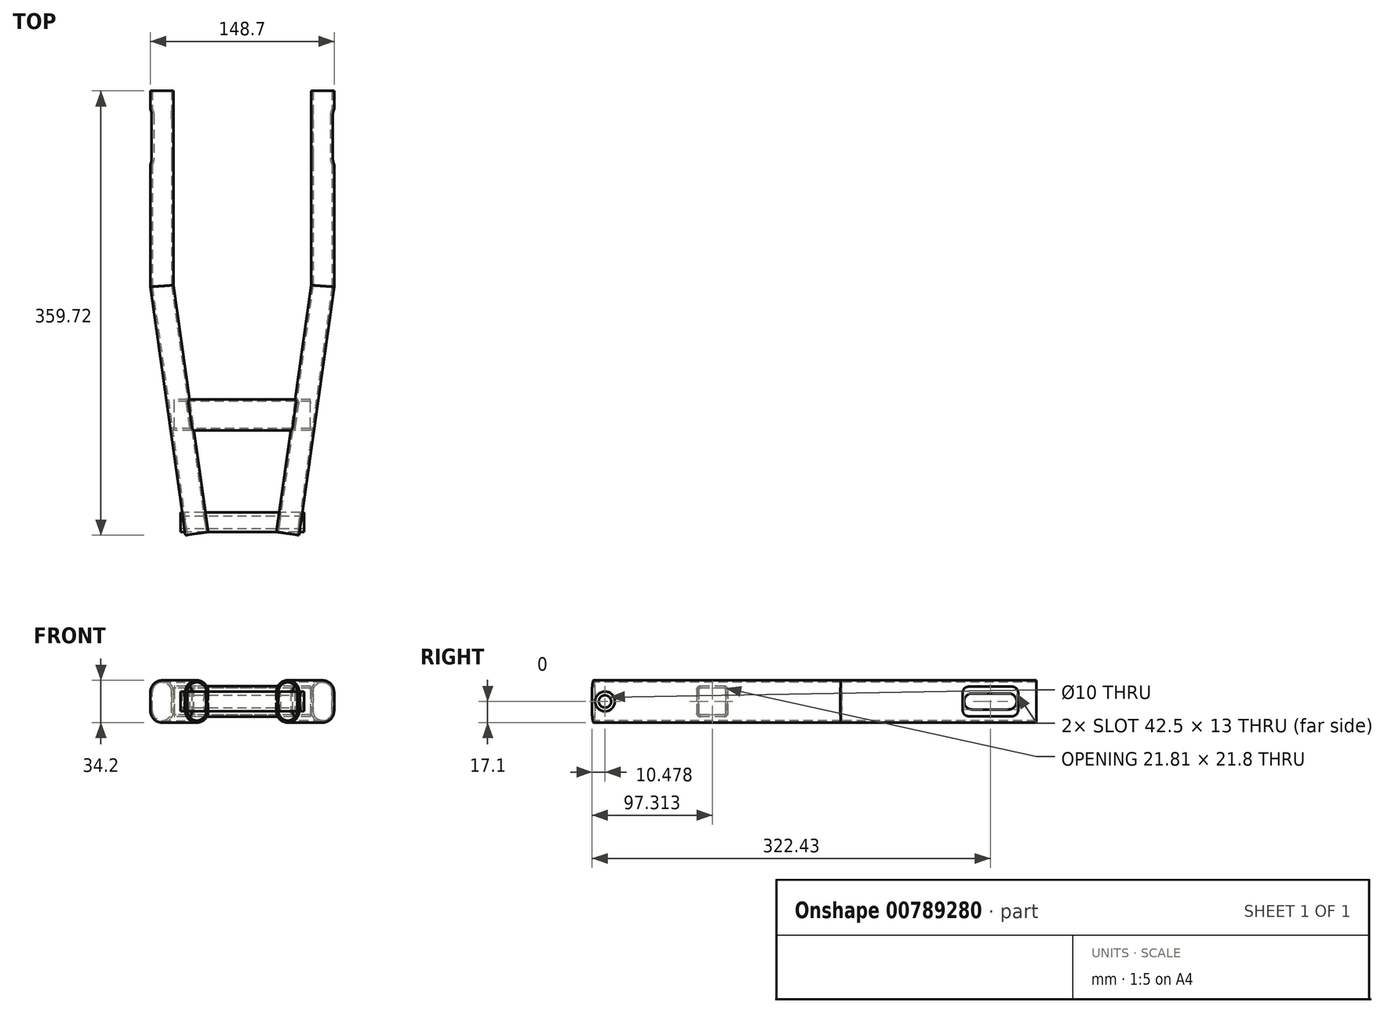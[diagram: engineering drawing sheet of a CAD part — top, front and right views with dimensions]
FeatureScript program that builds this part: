
annotation { "Feature Type Name" : "Feature", "Feature Type Description" : "" }
export const myFeature = defineFeature(function(context is Context, id is Id, definition is map)
    precondition{}
    {
        {
            var Q0;
            Q0=qCreatedBy(makeId("Front.planeOp"),FACE);
            var sketch = newSketch(context, id + "F0", { "sketchPlane" : qUnion([Q0])});
            skLineSegment(sketch, "E0.left", {"start": v(-57.25, -7.75) * mm, "end": v(-57.25, 7.75) * mm});
            skLineSegment(sketch, "E0.right", {"start": v(-72.75, -7.75) * mm, "end": v(-72.75, 7.75) * mm});
            skPoint(sketch, "E0.middle", {"position": v(-65, 0) * mm});
            skArc(sketch, "E1", {"start": v(-57.25, 7.75) * mm, "mid": v(-65, 15.5) * mm, "end": v(-72.75, 7.75) * mm});
            skArc(sketch, "E2", {"start": v(-72.75, -7.75) * mm, "mid": v(-65, -15.5) * mm, "end": v(-57.25, -7.75) * mm});
            skLineSegment(sketch, "E3", {"start": v(-55.65, 7.75) * mm, "end": v(-55.65, -7.75) * mm});
            skLineSegment(sketch, "E4", {"start": v(-74.35, 7.75) * mm, "end": v(-74.35, -7.75) * mm});
            skArc(sketch, "E5", {"start": v(-55.65, 7.75) * mm, "mid": v(-65, 17.1) * mm, "end": v(-74.35, 7.75) * mm});
            skArc(sketch, "E6", {"start": v(-74.35, -7.75) * mm, "mid": v(-65, -17.1) * mm, "end": v(-55.65, -7.75) * mm});
            skSolve(sketch);
        }
        {
            var Q0;
            Q0=qCreatedBy(makeId("Top.planeOp"),FACE);
            var sketch = newSketch(context, id + "F1", { "sketchPlane" : qUnion([Q0])});
            skLineSegment(sketch, "E7", {"start": v(-65, 0) * mm, "end": v(-65, -158.03) * mm});
            skLineSegment(sketch, "E8", {"start": v(-65, -158.03) * mm, "end": v(-36.84, -358.42) * mm});
            skSolve(sketch);
        }
        {
            var Q0;
            Q0 = qSketchRegion(id + "F0", true);
            var Q1;
            Q1=sQuery(id+"F1.wireOp",EDGE,"E7");
            var Q2;
            Q2=sQuery(id+"F1.wireOp",EDGE,"E8");
            sweep(context, id + "F2", {"profiles" : qUnion([Q0]), "path" : qUnion([Q1, Q2])});
        }
        {
            var Q0;
            Q0=makeQuery(id+"F2.opSweep","SWEPT_BODY",BODY,{"disambiguationData":[OSD([sQuery(id+"F0.wireOp",EDGE,"E0.left"),sQuery(id+"F0.wireOp",EDGE,"E0.right"),sQuery(id+"F0.wireOp",EDGE,"E1"),sQuery(id+"F0.wireOp",EDGE,"E2"),sQuery(id+"F0.wireOp",EDGE,"E3"),sQuery(id+"F0.wireOp",EDGE,"E4"),sQuery(id+"F0.wireOp",EDGE,"E5"),sQuery(id+"F0.wireOp",EDGE,"E6"),sQuery(id+"F1.wireOp",EDGE,"E8")])]});
            var Q1;
            Q1=qCreatedBy(makeId("Right.planeOp"),FACE);
            mirror(context, id + "F3", {"operationType" : NewBodyOperationType.ADD, "entities" : qUnion([Q0]), "mirrorPlane" : qUnion([Q1])});
        }
        {
            var Q0;
            Q0=qCreatedBy(makeId("Right.planeOp"),FACE);
            var sketch = newSketch(context, id + "F4", { "sketchPlane" : qUnion([Q0])});
            skCircle(sketch, "E9", {"center": v(-349.24, 0) * mm, "radius": 8 * mm});
            skSolve(sketch);
        }
        {
            var Q0;
            Q0 = qSketchRegion(id + "F4", true);
            extrude(context, id + "F5", {"entities" : qUnion([Q0]), "operationType" : NewBodyOperationType.ADD, "endBound" : BoundingType.SYMMETRIC, "depth" : 100 * mm, "offsetDistance" : 25 * mm});
        }
        {
            var Q0;
            Q0=makeQuery(id+"F5.opExtrude","CAP_FACE",FACE,{"disambiguationData":[OSD([sQuery(id+"F4.wireOp",EDGE,"E9")])],"isStart":false});
            var sketch = newSketch(context, id + "F6", { "sketchPlane" : qUnion([Q0])});
            skCircle(sketch, "E10", {"center": v(-349.24, 0) * mm, "radius": 5 * mm});
            skSolve(sketch);
        }
        {
            var Q0;
            Q0=makeQuery(id+"F6.imprint","IMPRINT",FACE,{"disambiguationData":[TD([[makeQuery(id+"F6.imprint","IMPRINT",EDGE,{"derivedFrom":sQuery(id+"F6.wireOp",EDGE,"E10")}),1.0]])]});
            extrude(context, id + "F7", {"entities" : qUnion([Q0]), "operationType" : NewBodyOperationType.REMOVE, "oppositeDirection" : true, "depth" : 100 * mm, "offsetDistance" : 25 * mm});
        }
        {
            var Q0;
            Q0=qCreatedBy(makeId("Right.planeOp"),FACE);
            var sketch = newSketch(context, id + "F8", { "sketchPlane" : qUnion([Q0])});
            skLineSegment(sketch, "E11.bottom", {"start": v(-271.91, 12.5) * mm, "end": v(-252.9, 12.5) * mm});
            skLineSegment(sketch, "E11.top", {"start": v(-271.91, -12.5) * mm, "end": v(-252.9, -12.5) * mm});
            skLineSegment(sketch, "E11.left", {"start": v(-274.91, 9.5) * mm, "end": v(-274.91, -9.5) * mm});
            skLineSegment(sketch, "E11.right", {"start": v(-249.9, 9.5) * mm, "end": v(-249.9, -9.5) * mm});
            skPoint(sketch, "E11.middle", {"position": v(-262.4, 0) * mm});
            skPoint(sketch, "E12.visualSharp", {"position": v(-249.9, 12.5) * mm});
            skArc(sketch, "E12.filletArc", {"start": v(-249.9, 9.5) * mm, "mid": v(-250.78, 11.62) * mm, "end": v(-252.9, 12.5) * mm});
            skPoint(sketch, "E13.visualSharp", {"position": v(-274.91, 12.5) * mm});
            skArc(sketch, "E13.filletArc", {"start": v(-271.91, 12.5) * mm, "mid": v(-274.03, 11.62) * mm, "end": v(-274.91, 9.5) * mm});
            skPoint(sketch, "E14.visualSharp", {"position": v(-274.91, -12.5) * mm});
            skArc(sketch, "E14.filletArc", {"start": v(-274.91, -9.5) * mm, "mid": v(-274.03, -11.62) * mm, "end": v(-271.91, -12.5) * mm});
            skPoint(sketch, "E15.visualSharp", {"position": v(-249.9, -12.5) * mm});
            skArc(sketch, "E15.filletArc", {"start": v(-252.9, -12.5) * mm, "mid": v(-250.78, -11.62) * mm, "end": v(-249.9, -9.5) * mm});
            skLineSegment(sketch, "E16.bottom", {"start": v(-271.91, 10.9) * mm, "end": v(-252.9, 10.9) * mm});
            skLineSegment(sketch, "E16.top", {"start": v(-271.91, -10.9) * mm, "end": v(-252.9, -10.9) * mm});
            skLineSegment(sketch, "E16.left", {"start": v(-273.31, 9.5) * mm, "end": v(-273.31, -9.5) * mm});
            skLineSegment(sketch, "E16.right", {"start": v(-251.5, 9.5) * mm, "end": v(-251.5, -9.5) * mm});
            skPoint(sketch, "E17.visualSharp", {"position": v(-251.5, 10.9) * mm});
            skArc(sketch, "E17.filletArc", {"start": v(-251.5, 9.5) * mm, "mid": v(-251.91, 10.49) * mm, "end": v(-252.9, 10.9) * mm});
            skPoint(sketch, "E18.visualSharp", {"position": v(-273.31, 10.9) * mm});
            skArc(sketch, "E18.filletArc", {"start": v(-271.91, 10.9) * mm, "mid": v(-272.9, 10.49) * mm, "end": v(-273.31, 9.5) * mm});
            skPoint(sketch, "E19.visualSharp", {"position": v(-273.31, -10.9) * mm});
            skArc(sketch, "E19.filletArc", {"start": v(-273.31, -9.5) * mm, "mid": v(-272.9, -10.49) * mm, "end": v(-271.91, -10.9) * mm});
            skPoint(sketch, "E20.visualSharp", {"position": v(-251.5, -10.9) * mm});
            skArc(sketch, "E20.filletArc", {"start": v(-252.9, -10.9) * mm, "mid": v(-251.91, -10.49) * mm, "end": v(-251.5, -9.5) * mm});
            skSolve(sketch);
        }
        {
            var Q0;
            Q0=makeQuery(id+"F8.imprint","IMPRINT",FACE,{"disambiguationData":[TD([[makeQuery(id+"F8.imprint","IMPRINT",EDGE,{"derivedFrom":sQuery(id+"F8.wireOp",EDGE,"E11.bottom")}),-1.0]])]});
            extrude(context, id + "F9", {"entities" : qUnion([Q0]), "operationType" : NewBodyOperationType.ADD, "endBound" : BoundingType.SYMMETRIC, "depth" : 110 * mm, "offsetDistance" : 25 * mm});
        }
        {
            var Q0;
            Q0=qCreatedBy(makeId("Right.planeOp"),FACE);
            var sketch = newSketch(context, id + "F10", { "sketchPlane" : qUnion([Q0])});
            skLineSegment(sketch, "E21.bottom", {"start": v(-52.04, -6.5) * mm, "end": v(-22.54, -6.5) * mm});
            skLineSegment(sketch, "E21.top", {"start": v(-52.04, 6.5) * mm, "end": v(-22.54, 6.5) * mm});
            skPoint(sketch, "E21.middle", {"position": v(-37.3, 0) * mm});
            skArc(sketch, "E22", {"start": v(-52.04, 6.5) * mm, "mid": v(-58.54, 0) * mm, "end": v(-52.04, -6.5) * mm});
            skArc(sketch, "E23", {"start": v(-22.54, -6.5) * mm, "mid": v(-16.04, 0) * mm, "end": v(-22.54, 6.5) * mm});
            skSolve(sketch);
        }
        {
            var Q0;
            Q0 = qSketchRegion(id + "F10", true);
            extrude(context, id + "F11", {"entities" : qUnion([Q0]), "operationType" : NewBodyOperationType.REMOVE, "endBound" : BoundingType.SYMMETRIC, "oppositeDirection" : true, "depth" : 120 * mm, "offsetDistance" : 25 * mm});
        }
        {
            var Q0;
            Q0=makeQuery(id+"F3.opPattern","COPY",FACE,{"derivedFrom":makeQuery(id+"F2.opSweep","SWEPT_FACE",FACE,{"disambiguationData":[OSD([sQuery(id+"F0.wireOp",EDGE,"E4"),sQuery(id+"F1.wireOp",EDGE,"E7")])]}),"instanceName":"1"});
            var sketch = newSketch(context, id + "F12", { "sketchPlane" : qUnion([Q0])});
            skLineSegment(sketch, "E24.bottom", {"start": v(-54.76, 12) * mm, "end": v(-19.76, 12) * mm});
            skLineSegment(sketch, "E24.top", {"start": v(-54.76, -12) * mm, "end": v(-19.76, -12) * mm});
            skLineSegment(sketch, "E24.left", {"start": v(-59.76, 7) * mm, "end": v(-59.76, -7) * mm});
            skLineSegment(sketch, "E24.right", {"start": v(-14.76, 7) * mm, "end": v(-14.76, -7) * mm});
            skPoint(sketch, "E24.middle", {"position": v(-37.26, 0) * mm});
            skPoint(sketch, "E25.visualSharp", {"position": v(-59.76, 12) * mm});
            skArc(sketch, "E25.filletArc", {"start": v(-54.76, 12) * mm, "mid": v(-58.3, 10.54) * mm, "end": v(-59.76, 7) * mm});
            skPoint(sketch, "E26.visualSharp", {"position": v(-14.76, 12) * mm});
            skArc(sketch, "E26.filletArc", {"start": v(-14.76, 7) * mm, "mid": v(-16.22, 10.54) * mm, "end": v(-19.76, 12) * mm});
            skPoint(sketch, "E27.visualSharp", {"position": v(-14.76, -12) * mm});
            skArc(sketch, "E27.filletArc", {"start": v(-19.76, -12) * mm, "mid": v(-16.22, -10.54) * mm, "end": v(-14.76, -7) * mm});
            skPoint(sketch, "E28.visualSharp", {"position": v(-59.76, -12) * mm});
            skArc(sketch, "E28.filletArc", {"start": v(-59.76, -7) * mm, "mid": v(-58.3, -10.54) * mm, "end": v(-54.76, -12) * mm});
            skSolve(sketch);
        }
        {
            var Q0;
            Q0 = qSketchRegion(id + "F12", true);
            extrude(context, id + "F13", {"entities" : qUnion([Q0]), "operationType" : NewBodyOperationType.REMOVE, "oppositeDirection" : true, "depth" : 10 * mm, "offsetDistance" : 25 * mm});
        }
        {
            var Q0;
            Q0=makeQuery(id+"F2.opSweep","SWEPT_FACE",FACE,{"disambiguationData":[OSD([sQuery(id+"F0.wireOp",EDGE,"E4"),sQuery(id+"F1.wireOp",EDGE,"E7")])]});
            var sketch = newSketch(context, id + "F14", { "sketchPlane" : qUnion([Q0])});
            skLineSegment(sketch, "E29.bottom", {"start": v(54.76, 12) * mm, "end": v(19.76, 12) * mm});
            skLineSegment(sketch, "E29.top", {"start": v(54.76, -12) * mm, "end": v(19.76, -12) * mm});
            skLineSegment(sketch, "E29.left", {"start": v(59.76, 7) * mm, "end": v(59.76, -7) * mm});
            skLineSegment(sketch, "E29.right", {"start": v(14.76, 7) * mm, "end": v(14.76, -7) * mm});
            skPoint(sketch, "E29.middle", {"position": v(37.26, 0) * mm});
            skPoint(sketch, "E30.visualSharp", {"position": v(59.76, 12) * mm});
            skArc(sketch, "E30.filletArc", {"start": v(59.76, 7) * mm, "mid": v(58.3, 10.54) * mm, "end": v(54.76, 12) * mm});
            skPoint(sketch, "E31.visualSharp", {"position": v(14.76, 12) * mm});
            skArc(sketch, "E31.filletArc", {"start": v(19.76, 12) * mm, "mid": v(16.22, 10.54) * mm, "end": v(14.76, 7) * mm});
            skPoint(sketch, "E32.visualSharp", {"position": v(14.76, -12) * mm});
            skArc(sketch, "E32.filletArc", {"start": v(14.76, -7) * mm, "mid": v(16.22, -10.54) * mm, "end": v(19.76, -12) * mm});
            skPoint(sketch, "E33.visualSharp", {"position": v(59.76, -12) * mm});
            skArc(sketch, "E33.filletArc", {"start": v(54.76, -12) * mm, "mid": v(58.3, -10.54) * mm, "end": v(59.76, -7) * mm});
            skSolve(sketch);
        }
        {
            var Q0;
            Q0 = qSketchRegion(id + "F14", true);
            extrude(context, id + "F15", {"entities" : qUnion([Q0]), "operationType" : NewBodyOperationType.REMOVE, "oppositeDirection" : true, "depth" : 10 * mm, "offsetDistance" : 25 * mm});
        }
    });
